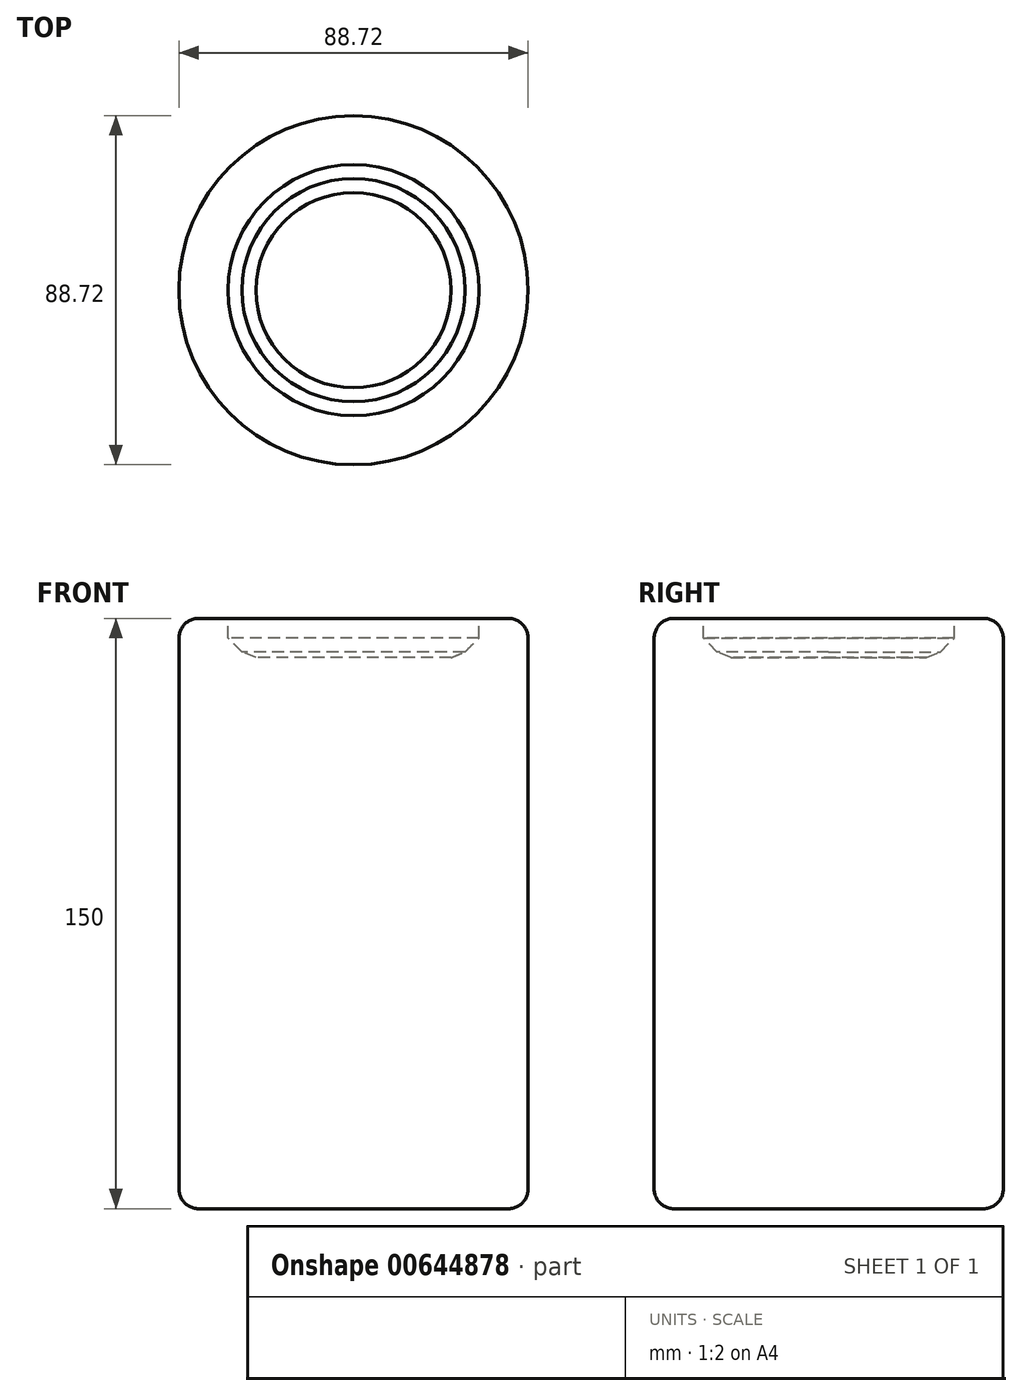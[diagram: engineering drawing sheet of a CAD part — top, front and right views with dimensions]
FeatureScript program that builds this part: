
annotation { "Feature Type Name" : "Feature", "Feature Type Description" : "" }
export const myFeature = defineFeature(function(context is Context, id is Id, definition is map)
    precondition{}
    {
        {
            var Q0;
            Q0=qCreatedBy(makeId("Top.planeOp"),FACE);
            var sketch = newSketch(context, id + "F0", { "sketchPlane" : qUnion([Q0])});
            skCircle(sketch, "E0", {"center": v(0, 0) * mm, "radius": 44.36 * mm});
            skSolve(sketch);
        }
        {
            var Q0;
            Q0 = qSketchRegion(id + "F0", true);
            extrude(context, id + "F1", {"entities" : qUnion([Q0]), "depth" : 150 * mm, "offsetDistance" : 25.4 * mm});
        }
        {
            var Q0;
            Q0=makeQuery(id+"F1.opExtrude","CAP_EDGE",EDGE,{"disambiguationData":[OSD([sQuery(id+"F0.wireOp",EDGE,"E0")])],"isStart":false});
            fillet(context, id + "F2", {"entities" : qUnion([Q0]), "radius" : 5.08 * mm, "tangentPropagation" : true, "allowEdgeOverflow" : false});
        }
        {
            var Q0;
            Q0=makeQuery(id+"F1.opExtrude","CAP_FACE",FACE,{"disambiguationData":[OSD([sQuery(id+"F0.wireOp",EDGE,"E0")])],"isStart":false});
            var sketch = newSketch(context, id + "F3", { "sketchPlane" : qUnion([Q0])});
            skCircle(sketch, "E1", {"center": v(0, 0) * mm, "radius": 31.48 * mm});
            skSolve(sketch);
        }
        {
            var Q0;
            Q0 = qSketchRegion(id + "F3", true);
            extrude(context, id + "F4", {"entities" : qUnion([Q0]), "operationType" : NewBodyOperationType.ADD, "oppositeDirection" : true, "depth" : 20 * mm, "offsetDistance" : 25 * mm});
        }
        {
            var Q0;
            Q0=makeQuery(id+"F1.opExtrude","CAP_FACE",FACE,{"disambiguationData":[OSD([sQuery(id+"F0.wireOp",EDGE,"E0")])],"isStart":false});
            var sketch = newSketch(context, id + "F5", { "sketchPlane" : qUnion([Q0])});
            skCircle(sketch, "E2", {"center": v(0, 0) * mm, "radius": 31.88 * mm});
            skSolve(sketch);
        }
        {
            var Q0;
            Q0=makeQuery(id+"F5.imprint","IMPRINT",FACE,{"disambiguationData":[TD([[makeQuery(id+"F5.imprint","IMPRINT",EDGE,{"derivedFrom":sQuery(id+"F5.wireOp",EDGE,"E2")}),1.0]])]});
            extrude(context, id + "F6", {"entities" : qUnion([Q0]), "operationType" : NewBodyOperationType.REMOVE, "oppositeDirection" : true, "depth" : 10 * mm, "offsetDistance" : 25 * mm});
        }
        {
            var Q0;
            Q0=makeQuery(id+"F6.boolean.opBoolean","COPY",FACE,{"derivedFrom":makeQuery(id+"F6.opExtrude","CAP_FACE",FACE,{"disambiguationData":[OSD([sQuery(id+"F5.wireOp",EDGE,"E2")])],"isStart":false})});
            chamfer(context, id + "F7", {"entities" : qUnion([Q0]), "width" : 5 * mm, "tangentPropagation" : true});
        }
        {
            var Q0;
            Q0=makeQuery(id+"F6.boolean.opBoolean","COPY",FACE,{"derivedFrom":makeQuery(id+"F6.opExtrude","CAP_FACE",FACE,{"disambiguationData":[OSD([sQuery(id+"F5.wireOp",EDGE,"E2")])],"isStart":false})});
            chamfer(context, id + "F8", {"entities" : qUnion([Q0]), "width" : 5 * mm, "tangentPropagation" : true});
        }
        {
            var Q0;
            Q0=makeQuery(id+"F1.opExtrude","CAP_EDGE",EDGE,{"disambiguationData":[OSD([sQuery(id+"F0.wireOp",EDGE,"E0")])],"isStart":true});
            fillet(context, id + "F9", {"entities" : qUnion([Q0]), "radius" : 5 * mm, "tangentPropagation" : true, "allowEdgeOverflow" : false});
        }
        {
            var Q0;
            Q0=makeQuery(id+"F1.opExtrude","CAP_FACE",FACE,{"disambiguationData":[OSD([sQuery(id+"F0.wireOp",EDGE,"E0")])],"isStart":true});
            var sketch = newSketch(context, id + "F10", { "sketchPlane" : qUnion([Q0])});
            skCircle(sketch, "E3", {"center": v(0, 0) * mm, "radius": 31.44 * mm});
            skSolve(sketch);
        }
        {
            var Q0;
            Q0 = qSketchRegion(id + "F10", true);
            extrude(context, id + "F11", {"entities" : qUnion([Q0]), "operationType" : NewBodyOperationType.ADD, "oppositeDirection" : true, "depth" : 25 * mm, "offsetDistance" : 25 * mm});
        }
        {
            var Q0;
            Q0=makeQuery(id+"F1.opExtrude","CAP_FACE",FACE,{"disambiguationData":[OSD([sQuery(id+"F0.wireOp",EDGE,"E0")])],"isStart":true});
            var sketch = newSketch(context, id + "F12", { "sketchPlane" : qUnion([Q0])});
            skCircle(sketch, "E4", {"center": v(0, 0) * mm, "radius": 31.79 * mm});
            skSolve(sketch);
        }
        {
            var Q0;
            Q0 = qSketchRegion(id + "F12", true);
            extrude(context, id + "F13", {"entities" : qUnion([Q0]), "operationType" : NewBodyOperationType.ADD, "depth" : -25 * mm, "offsetDistance" : 25 * mm});
        }
        {
            var Q0;
            Q0=makeQuery(id+"F1.opExtrude","CAP_FACE",FACE,{"disambiguationData":[OSD([sQuery(id+"F0.wireOp",EDGE,"E0")])],"isStart":true});
            var sketch = newSketch(context, id + "F14", { "sketchPlane" : qUnion([Q0])});
            skCircle(sketch, "E5", {"center": v(0, 0) * mm, "radius": 32.19 * mm});
            skSolve(sketch);
        }
        {
            var Q0;
            Q0 = qSketchRegion(id + "F14", true);
            extrude(context, id + "F15", {"entities" : qUnion([Q0]), "operationType" : NewBodyOperationType.ADD, "depth" : -25 * mm, "offsetDistance" : 25 * mm});
        }
    });
